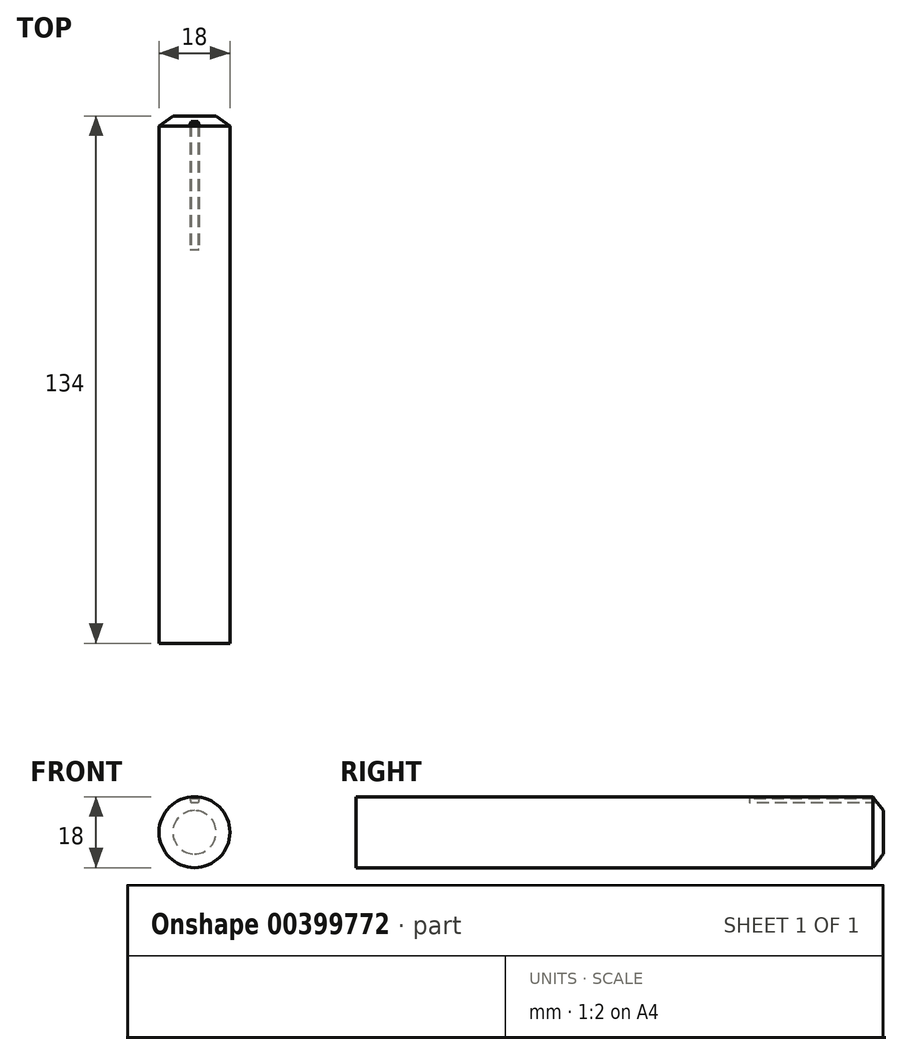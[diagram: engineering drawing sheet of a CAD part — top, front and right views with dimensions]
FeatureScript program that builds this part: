
annotation { "Feature Type Name" : "Feature", "Feature Type Description" : "" }
export const myFeature = defineFeature(function(context is Context, id is Id, definition is map)
    precondition{}
    {
        {
            var Q0;
            Q0=qCreatedBy(makeId("Front.planeOp"),FACE);
            var sketch = newSketch(context, id + "F0", { "sketchPlane" : qUnion([Q0])});
            skCircle(sketch, "E0", {"center": v(0, 0) * mm, "radius": 9 * mm});
            skSolve(sketch);
        }
        {
            var Q0;
            Q0 = qSketchRegion(id + "F0", true);
            extrude(context, id + "F1", {"entities" : qUnion([Q0]), "oppositeDirection" : true, "depth" : 100 * mm});
        }
        {
            var Q0;
            Q0=makeQuery(id+"F1.opExtrude","CAP_FACE",FACE,{"disambiguationData":[OSD([sQuery(id+"F0.wireOp",EDGE,"E0")])],"isStart":false});
            var sketch = newSketch(context, id + "F2", { "sketchPlane" : qUnion([Q0])});
            skLineSegment(sketch, "E1", {"start": v(0, 11.92) * mm, "end": v(0, -14.97) * mm, "construction": true});
            skLineSegment(sketch, "E2", {"start": v(-16.83, 0) * mm, "end": v(25.4, 0) * mm, "construction": true});
            skCircle(sketch, "E3", {"center": v(0, 0) * mm, "radius": 7.5 * mm});
            skPoint(sketch, "E4", {"position": v(0.88, 7.45) * mm});
            skSolve(sketch);
        }
        {
            var Q0;
            Q0 = qSketchRegion(id + "F2", true);
            extrude(context, id + "F3", {"entities" : qUnion([Q0]), "operationType" : NewBodyOperationType.ADD, "depth" : 34 * mm});
        }
        {
            var Q0;
            Q0=makeQuery(id+"F1.opExtrude","CAP_FACE",FACE,{"disambiguationData":[OSD([sQuery(id+"F0.wireOp",EDGE,"E0")])],"isStart":false});
            var sketch = newSketch(context, id + "F4", { "sketchPlane" : qUnion([Q0])});
            skCircle(sketch, "E5.0", {"center": v(0, 0) * mm, "radius": 7.5 * mm});
            skLineSegment(sketch, "E6", {"start": v(0, 0) * mm, "end": v(0, 14.47) * mm, "construction": true});
            skArc(sketch, "E7", {"start": v(-1.17, 8.42) * mm, "mid": v(0, 8.5) * mm, "end": v(1.17, 8.42) * mm});
            skLineSegment(sketch, "E8", {"start": v(-1.17, 8.42) * mm, "end": v(-0.88, 7.45) * mm});
            skLineSegment(sketch, "E9", {"start": v(1.17, 8.42) * mm, "end": v(0.88, 7.45) * mm});
            skLineSegment(sketch, "E10.1.0", {"start": v(-5.53, 6.45) * mm, "end": v(-4.77, 5.79) * mm});
            skArc(sketch, "E10.1.1", {"start": v(-5.53, 6.45) * mm, "mid": v(-4.6, 7.15) * mm, "end": v(-3.57, 7.71) * mm});
            skLineSegment(sketch, "E10.1.2", {"start": v(-3.57, 7.71) * mm, "end": v(-3.28, 6.74) * mm});
            skLineSegment(sketch, "E10.2.0", {"start": v(-8.14, 2.43) * mm, "end": v(-7.14, 2.3) * mm});
            skArc(sketch, "E10.2.1", {"start": v(-8.14, 2.43) * mm, "mid": v(-7.73, 3.53) * mm, "end": v(-7.17, 4.56) * mm});
            skLineSegment(sketch, "E10.2.2", {"start": v(-7.17, 4.56) * mm, "end": v(-6.4, 3.9) * mm});
            skLineSegment(sketch, "E10.3.0", {"start": v(-8.17, -2.35) * mm, "end": v(-7.25, -1.93) * mm});
            skArc(sketch, "E10.3.1", {"start": v(-8.17, -2.35) * mm, "mid": v(-8.41, -1.2) * mm, "end": v(-8.5, -0.04) * mm});
            skLineSegment(sketch, "E10.3.2", {"start": v(-8.5, -0.04) * mm, "end": v(-7.5, -0.19) * mm});
            skLineSegment(sketch, "E10.4.0", {"start": v(-5.6, -6.4) * mm, "end": v(-5.05, -5.55) * mm});
            skArc(sketch, "E10.4.1", {"start": v(-5.6, -6.4) * mm, "mid": v(-6.42, -5.57) * mm, "end": v(-7.13, -4.63) * mm});
            skLineSegment(sketch, "E10.4.2", {"start": v(-7.13, -4.63) * mm, "end": v(-6.2, -4.2) * mm});
            skLineSegment(sketch, "E10.5.0", {"start": v(-1.25, -8.4) * mm, "end": v(-1.25, -7.4) * mm});
            skArc(sketch, "E10.5.1", {"start": v(-1.25, -8.4) * mm, "mid": v(-2.4, -8.15) * mm, "end": v(-3.5, -7.75) * mm});
            skLineSegment(sketch, "E10.5.2", {"start": v(-3.5, -7.75) * mm, "end": v(-2.95, -6.9) * mm});
            skLineSegment(sketch, "E10.6.0", {"start": v(3.5, -7.75) * mm, "end": v(2.95, -6.9) * mm});
            skArc(sketch, "E10.6.1", {"start": v(3.5, -7.75) * mm, "mid": v(2.4, -8.15) * mm, "end": v(1.25, -8.4) * mm});
            skLineSegment(sketch, "E10.6.2", {"start": v(1.25, -8.4) * mm, "end": v(1.25, -7.4) * mm});
            skLineSegment(sketch, "E10.7.0", {"start": v(7.13, -4.63) * mm, "end": v(6.2, -4.2) * mm});
            skArc(sketch, "E10.7.1", {"start": v(7.13, -4.63) * mm, "mid": v(6.42, -5.57) * mm, "end": v(5.6, -6.4) * mm});
            skLineSegment(sketch, "E10.7.2", {"start": v(5.6, -6.4) * mm, "end": v(5.05, -5.55) * mm});
            skLineSegment(sketch, "E10.8.0", {"start": v(8.5, -0.04) * mm, "end": v(7.5, -0.19) * mm});
            skArc(sketch, "E10.8.1", {"start": v(8.5, -0.04) * mm, "mid": v(8.41, -1.2) * mm, "end": v(8.17, -2.35) * mm});
            skLineSegment(sketch, "E10.8.2", {"start": v(8.17, -2.35) * mm, "end": v(7.25, -1.93) * mm});
            skLineSegment(sketch, "E10.9.0", {"start": v(7.17, 4.56) * mm, "end": v(6.4, 3.9) * mm});
            skArc(sketch, "E10.9.1", {"start": v(7.17, 4.56) * mm, "mid": v(7.73, 3.53) * mm, "end": v(8.14, 2.43) * mm});
            skLineSegment(sketch, "E10.9.2", {"start": v(8.14, 2.43) * mm, "end": v(7.14, 2.3) * mm});
            skLineSegment(sketch, "E10.10.0", {"start": v(3.57, 7.71) * mm, "end": v(3.28, 6.74) * mm});
            skArc(sketch, "E10.10.1", {"start": v(3.57, 7.71) * mm, "mid": v(4.6, 7.15) * mm, "end": v(5.53, 6.45) * mm});
            skLineSegment(sketch, "E10.10.2", {"start": v(5.53, 6.45) * mm, "end": v(4.77, 5.79) * mm});
            skSolve(sketch);
        }
        {
            var Q0;
            Q0=makeQuery(id+"F3.opExtrude","CAP_EDGE",EDGE,{"disambiguationData":[OSD([sQuery(id+"F2.wireOp",EDGE,"E3")])],"isStart":false});
            chamfer(context, id + "F5", {"entities" : qUnion([Q0]), "chamferType" : ChamferType.TWO_OFFSETS, "width1" : 2 * mm, "oppositeDirection" : false, "width2" : 1.5 * mm, "tangentPropagation" : true});
        }
        {
            var Q0;
            {var subQ0=sQuery(id+"F4.wireOp",EDGE,"E10.9.0");Q0=makeQuery(id+"F4.imprint","IMPRINT",FACE,{"disambiguationData":[TD([[makeQuery(id+"F4.imprint","IMPRINT",EDGE,{"derivedFrom":subQ0}),1.0]])]});}
            var Q1;
            {var subQ0=sQuery(id+"F4.wireOp",EDGE,"E10.10.0");Q1=makeQuery(id+"F4.imprint","IMPRINT",FACE,{"disambiguationData":[TD([[makeQuery(id+"F4.imprint","IMPRINT",EDGE,{"derivedFrom":subQ0}),1.0]])]});}
            var Q2;
            Q2=makeQuery(id+"F4.imprint","IMPRINT",FACE,{"disambiguationData":[TD([[makeQuery(id+"F4.imprint","IMPRINT",EDGE,{"derivedFrom":sQuery(id+"F4.wireOp",EDGE,"E7")}),-1.0]])]});
            var Q3;
            {var subQ0=sQuery(id+"F4.wireOp",EDGE,"E10.1.0");Q3=makeQuery(id+"F4.imprint","IMPRINT",FACE,{"disambiguationData":[TD([[makeQuery(id+"F4.imprint","IMPRINT",EDGE,{"derivedFrom":subQ0}),1.0]])]});}
            var Q4;
            {var subQ0=sQuery(id+"F4.wireOp",EDGE,"E10.2.0");Q4=makeQuery(id+"F4.imprint","IMPRINT",FACE,{"disambiguationData":[TD([[makeQuery(id+"F4.imprint","IMPRINT",EDGE,{"derivedFrom":subQ0}),1.0]])]});}
            var Q5;
            {var subQ0=sQuery(id+"F4.wireOp",EDGE,"E10.3.0");Q5=makeQuery(id+"F4.imprint","IMPRINT",FACE,{"disambiguationData":[TD([[makeQuery(id+"F4.imprint","IMPRINT",EDGE,{"derivedFrom":subQ0}),1.0]])]});}
            var Q6;
            {var subQ0=sQuery(id+"F4.wireOp",EDGE,"E10.4.0");Q6=makeQuery(id+"F4.imprint","IMPRINT",FACE,{"disambiguationData":[TD([[makeQuery(id+"F4.imprint","IMPRINT",EDGE,{"derivedFrom":subQ0}),1.0]])]});}
            var Q7;
            {var subQ0=sQuery(id+"F4.wireOp",EDGE,"E10.5.0");Q7=makeQuery(id+"F4.imprint","IMPRINT",FACE,{"disambiguationData":[TD([[makeQuery(id+"F4.imprint","IMPRINT",EDGE,{"derivedFrom":subQ0}),1.0]])]});}
            var Q8;
            {var subQ0=sQuery(id+"F4.wireOp",EDGE,"E10.6.0");Q8=makeQuery(id+"F4.imprint","IMPRINT",FACE,{"disambiguationData":[TD([[makeQuery(id+"F4.imprint","IMPRINT",EDGE,{"derivedFrom":subQ0}),1.0]])]});}
            var Q9;
            {var subQ0=sQuery(id+"F4.wireOp",EDGE,"E10.7.0");Q9=makeQuery(id+"F4.imprint","IMPRINT",FACE,{"disambiguationData":[TD([[makeQuery(id+"F4.imprint","IMPRINT",EDGE,{"derivedFrom":subQ0}),1.0]])]});}
            var Q10;
            {var subQ0=sQuery(id+"F4.wireOp",EDGE,"E10.8.0");Q10=makeQuery(id+"F4.imprint","IMPRINT",FACE,{"disambiguationData":[TD([[makeQuery(id+"F4.imprint","IMPRINT",EDGE,{"derivedFrom":subQ0}),1.0]])]});}
            var Q11;
            Q11=makeQuery(id+"F5.opChamfer","BLEND_FACE",FACE,{"disambiguationData":[OSD([sQuery(id+"F2.wireOp",EDGE,"E3")])]});
            extrude(context, id + "F6", {"entities" : qUnion([Q0, Q1, Q2, Q3, Q4, Q5, Q6, Q7, Q8, Q9, Q10]), "operationType" : NewBodyOperationType.ADD, "endBound" : BoundingType.UP_TO_SURFACE, "endBoundEntityFace" : qUnion([Q11]), "depth" : 25.4 * mm});
        }
    });
